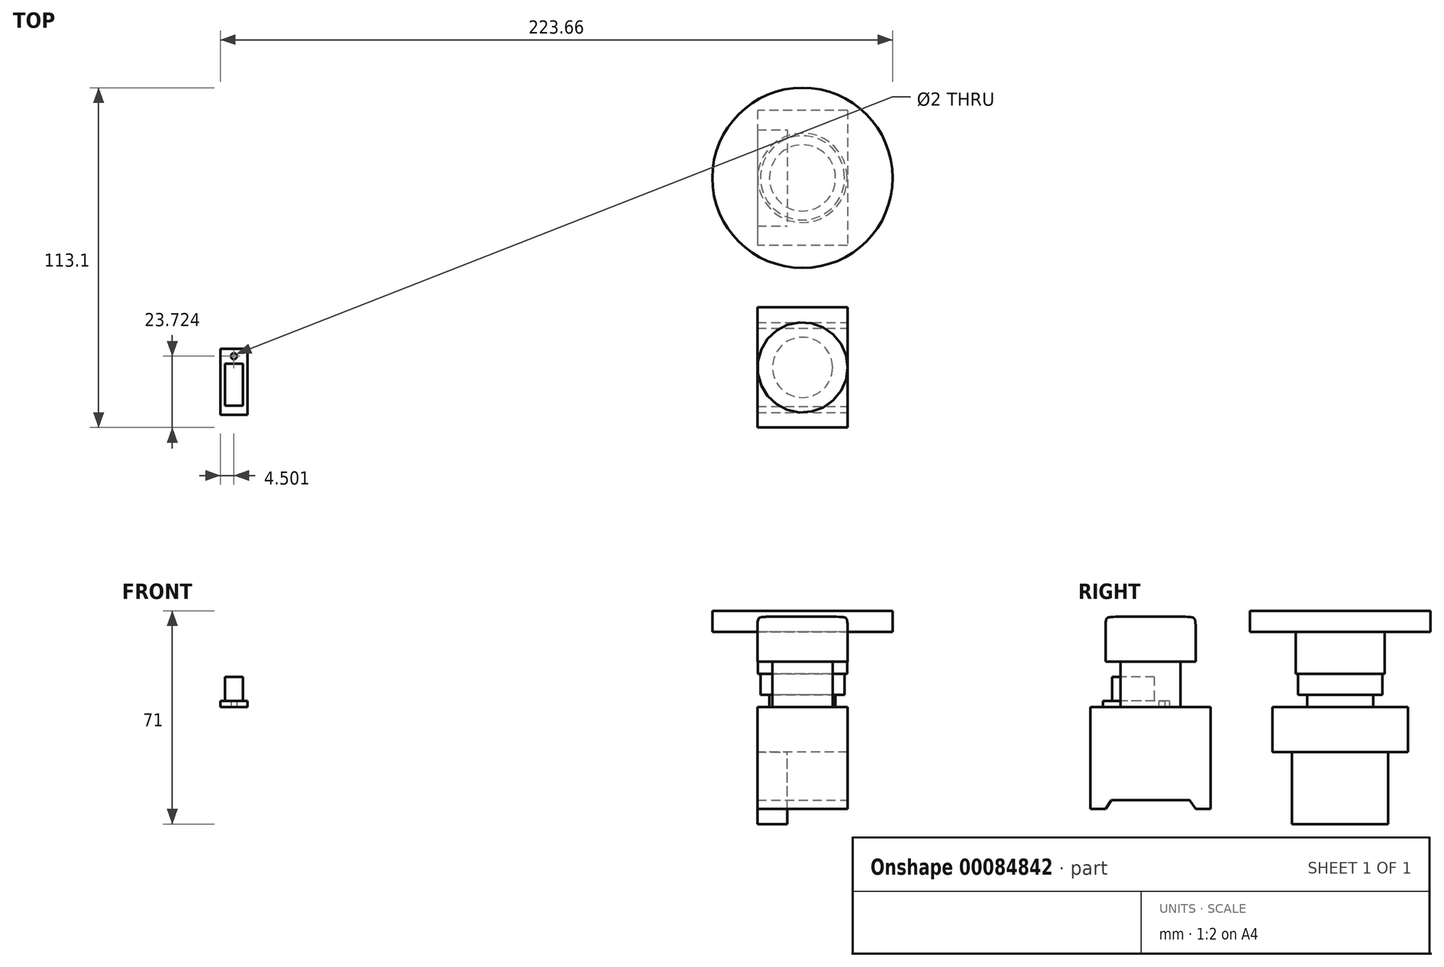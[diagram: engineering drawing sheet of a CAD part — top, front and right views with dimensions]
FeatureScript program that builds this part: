
annotation { "Feature Type Name" : "Feature", "Feature Type Description" : "" }
export const myFeature = defineFeature(function(context is Context, id is Id, definition is map)
    precondition{}
    {
        {
            var Q0;
            Q0=qCreatedBy(makeId("Front.planeOp"),FACE);
            var sketch = newSketch(context, id + "F0", { "sketchPlane" : qUnion([Q0])});
            skLineSegment(sketch, "E0", {"start": v(0, 0) * mm, "end": v(10, 0) * mm});
            skLineSegment(sketch, "E1", {"start": v(10, 0) * mm, "end": v(10, 15) * mm});
            skLineSegment(sketch, "E2", {"start": v(10, 15) * mm, "end": v(15, 15) * mm});
            skLineSegment(sketch, "E3", {"start": v(15, 15) * mm, "end": v(15, 30) * mm});
            skLineSegment(sketch, "E4", {"start": v(15, 30) * mm, "end": v(0, 30) * mm});
            skLineSegment(sketch, "E5", {"start": v(0, 30) * mm, "end": v(0, 0) * mm});
            skSolve(sketch);
        }
        {
            var Q0;
            Q0=qSketchRegion(id+"F0",true);
            var Q1;
            Q1=sQuery(id+"F0.wireOp",EDGE,"E5");
            revolve(context, id + "F1", {"entities" : qUnion([Q0]), "axis" : qUnion([Q1]), "revolveType" : RevolveType.FULL});
        }
        {
            var Q0;
            Q0=makeQuery(id+"F1.opRevolve","SWEPT_EDGE",EDGE,{"disambiguationData":[OSD([sQuery(id+"F0.wireOp",EDGE,"E3"),sQuery(id+"F0.wireOp",EDGE,"E4")])]});
            fillet(context, id + "F2", {"entities" : qUnion([Q0]), "radius" : 5 * mm, "tangentPropagation" : true, "rho" : 0.8, "crossSection" : FilletCrossSection.CONIC, "allowEdgeOverflow" : false});
        }
        {
            var Q0;
            Q0=qCreatedBy(makeId("Top.planeOp"),FACE);
            var sketch = newSketch(context, id + "F3", { "sketchPlane" : qUnion([Q0])});
            skLineSegment(sketch, "E6.rect.bottom", {"start": v(15, 20) * mm, "end": v(-15, 20) * mm});
            skLineSegment(sketch, "E6.rect.top", {"start": v(15, -20) * mm, "end": v(-15, -20) * mm});
            skLineSegment(sketch, "E6.rect.left", {"start": v(15, 20) * mm, "end": v(15, -20) * mm});
            skLineSegment(sketch, "E6.rect.right", {"start": v(-15, 20) * mm, "end": v(-15, -20) * mm});
            skPoint(sketch, "E6.rect.middle", {"position": v(0, 0) * mm});
            skSolve(sketch);
        }
        {
            var Q0;
            Q0=qSketchRegion(id+"F3",true);
            extrude(context, id + "F4", {"entities" : qUnion([Q0]), "operationType" : NewBodyOperationType.ADD, "oppositeDirection" : true, "depth" : 34 * mm});
        }
        {
            var Q0;
            Q0=makeQuery(id+"F4.opExtrude","SWEPT_FACE",FACE,{"disambiguationData":[OSD([sQuery(id+"F3.wireOp",EDGE,"E6.rect.left")])]});
            var sketch = newSketch(context, id + "F5", { "sketchPlane" : qUnion([Q0])});
            skLineSegment(sketch, "E7", {"start": v(0, -34) * mm, "end": v(-15, -34) * mm});
            skLineSegment(sketch, "E8", {"start": v(-15, -34) * mm, "end": v(-13, -31) * mm});
            skLineSegment(sketch, "E9", {"start": v(-13, -31) * mm, "end": v(0, -31) * mm});
            skLineSegment(sketch, "E10.MirrorCS", {"start": v(0, -34) * mm, "end": v(15, -34) * mm});
            skLineSegment(sketch, "E11.MirrorCS", {"start": v(13, -31) * mm, "end": v(0, -31) * mm});
            skLineSegment(sketch, "E12.MirrorCS", {"start": v(15, -34) * mm, "end": v(13, -31) * mm});
            skSolve(sketch);
        }
        {
            var Q0;
            Q0=qSketchRegion(id+"F5",true);
            extrude(context, id + "F6", {"entities" : qUnion([Q0]), "operationType" : NewBodyOperationType.REMOVE, "oppositeDirection" : true, "depth" : 34 * mm});
        }
        {
            var Q0;
            Q0=qCreatedBy(makeId("Top.planeOp"),FACE);
            var sketch = newSketch(context, id + "F7", { "sketchPlane" : qUnion([Q0])});
            skLineSegment(sketch, "E13.bottom", {"start": v(-193.66, 6.22) * mm, "end": v(-184.66, 6.22) * mm});
            skLineSegment(sketch, "E13.top", {"start": v(-193.66, -15.78) * mm, "end": v(-184.66, -15.78) * mm});
            skLineSegment(sketch, "E13.left", {"start": v(-193.66, 6.22) * mm, "end": v(-193.66, -15.78) * mm});
            skLineSegment(sketch, "E13.right", {"start": v(-184.66, 6.22) * mm, "end": v(-184.66, -15.78) * mm});
            skPoint(sketch, "E14", {"position": v(-189.16, 6.22) * mm});
            skLineSegment(sketch, "E15", {"start": v(-189.16, 6.22) * mm, "end": v(-189.16, 0.64) * mm, "construction": true});
            skCircle(sketch, "E16", {"center": v(-189.16, 3.72) * mm, "radius": 1 * mm});
            skSolve(sketch);
        }
        {
            var Q0;
            Q0=qSketchRegion(id+"F7",true);
            extrude(context, id + "F8", {"entities" : qUnion([Q0]), "depth" : 2 * mm});
        }
        {
            var Q0;
            Q0=makeQuery(id+"F8.opExtrude","CAP_FACE",FACE,{"disambiguationData":[OSD([sQuery(id+"F7.wireOp",EDGE,"E13.bottom"),sQuery(id+"F7.wireOp",EDGE,"E13.top"),sQuery(id+"F7.wireOp",EDGE,"E13.left"),sQuery(id+"F7.wireOp",EDGE,"E13.right")])],"isStart":false});
            var sketch = newSketch(context, id + "F9", { "sketchPlane" : qUnion([Q0])});
            skLineSegment(sketch, "E17", {"start": v(-193.66, -5.78) * mm, "end": v(-184.66, -5.78) * mm, "construction": true});
            skPoint(sketch, "E18", {"position": v(-189.16, -5.78) * mm});
            skLineSegment(sketch, "E19.rect.bottom", {"start": v(-186.16, 1.22) * mm, "end": v(-192.16, 1.22) * mm});
            skLineSegment(sketch, "E19.rect.top", {"start": v(-186.16, -12.78) * mm, "end": v(-192.16, -12.78) * mm});
            skLineSegment(sketch, "E19.rect.left", {"start": v(-186.16, 1.22) * mm, "end": v(-186.16, -12.78) * mm});
            skLineSegment(sketch, "E19.rect.right", {"start": v(-192.16, 1.22) * mm, "end": v(-192.16, -12.78) * mm});
            skSolve(sketch);
        }
        {
            var Q0;
            Q0=makeQuery(id+"F9.imprint","IMPRINT",FACE,{"disambiguationData":[TD([[makeQuery(id+"F9.imprint","IMPRINT",EDGE,{"derivedFrom":sQuery(id+"F9.wireOp",EDGE,"E19.rect.bottom")}),1.0]])]});
            extrude(context, id + "F10", {"entities" : qUnion([Q0]), "operationType" : NewBodyOperationType.ADD, "depth" : 8 * mm});
        }
        {
            var Q0;
            Q0=qCreatedBy(makeId("Top.planeOp"),FACE);
            var sketch = newSketch(context, id + "F11", { "sketchPlane" : qUnion([Q0])});
            skLineSegment(sketch, "E20.bottom", {"start": v(15, 85.6) * mm, "end": v(-15, 85.6) * mm});
            skLineSegment(sketch, "E20.top", {"start": v(15, 40.6) * mm, "end": v(-15, 40.6) * mm});
            skLineSegment(sketch, "E20.left", {"start": v(15, 85.6) * mm, "end": v(15, 40.6) * mm});
            skLineSegment(sketch, "E20.right", {"start": v(-15, 85.6) * mm, "end": v(-15, 40.6) * mm});
            skPoint(sketch, "E20.middle", {"position": v(0, 63.1) * mm});
            skSolve(sketch);
        }
        {
            var Q0;
            Q0=qSketchRegion(id+"F11",true);
            extrude(context, id + "F12", {"entities" : qUnion([Q0]), "oppositeDirection" : true, "depth" : 15 * mm});
        }
        {
            var Q0;
            Q0=makeQuery(id+"F12.opExtrude","CAP_FACE",FACE,{"disambiguationData":[OSD([sQuery(id+"F11.wireOp",EDGE,"E20.bottom"),sQuery(id+"F11.wireOp",EDGE,"E20.top"),sQuery(id+"F11.wireOp",EDGE,"E20.left"),sQuery(id+"F11.wireOp",EDGE,"E20.right")])],"isStart":false});
            var sketch = newSketch(context, id + "F13", { "sketchPlane" : qUnion([Q0])});
            skLineSegment(sketch, "E21", {"start": v(-15, -63.1) * mm, "end": v(15, -63.1) * mm, "construction": true});
            skLineSegment(sketch, "E22.bottom", {"start": v(-15, -79.1) * mm, "end": v(-5, -79.1) * mm});
            skLineSegment(sketch, "E22.top", {"start": v(-15, -47.1) * mm, "end": v(-5, -47.1) * mm});
            skLineSegment(sketch, "E22.left", {"start": v(-15, -79.1) * mm, "end": v(-15, -47.1) * mm});
            skLineSegment(sketch, "E22.right", {"start": v(-5, -79.1) * mm, "end": v(-5, -47.1) * mm});
            skPoint(sketch, "E22.middle", {"position": v(-10, -63.1) * mm});
            skSolve(sketch);
        }
        {
            var Q0;
            Q0=qSketchRegion(id+"F13",true);
            extrude(context, id + "F14", {"entities" : qUnion([Q0]), "operationType" : NewBodyOperationType.ADD, "depth" : 24 * mm});
        }
        {
            var Q0;
            Q0=makeQuery(id+"F12.opExtrude","CAP_FACE",FACE,{"disambiguationData":[OSD([sQuery(id+"F11.wireOp",EDGE,"E20.bottom"),sQuery(id+"F11.wireOp",EDGE,"E20.top"),sQuery(id+"F11.wireOp",EDGE,"E20.left"),sQuery(id+"F11.wireOp",EDGE,"E20.right")])],"isStart":true});
            var sketch = newSketch(context, id + "F15", { "sketchPlane" : qUnion([Q0])});
            skLineSegment(sketch, "E23", {"start": v(0, 85.6) * mm, "end": v(0, 40.6) * mm, "construction": true});
            skLineSegment(sketch, "E24", {"start": v(-15, 63.1) * mm, "end": v(15, 63.1) * mm, "construction": true});
            skPoint(sketch, "E25", {"position": v(0, 63.1) * mm});
            skCircle(sketch, "E26", {"center": v(0, 63.1) * mm, "radius": 11 * mm});
            skSolve(sketch);
        }
        {
            var Q0;
            Q0=qSketchRegion(id+"F15",true);
            extrude(context, id + "F16", {"entities" : qUnion([Q0]), "operationType" : NewBodyOperationType.ADD, "depth" : 4 * mm});
        }
        {
            var Q0;
            Q0=makeQuery(id+"F16.opExtrude","CAP_FACE",FACE,{"disambiguationData":[OSD([sQuery(id+"F15.wireOp",EDGE,"E26")])],"isStart":false});
            var sketch = newSketch(context, id + "F17", { "sketchPlane" : qUnion([Q0])});
            skPoint(sketch, "E27", {"position": v(0, 63.1) * mm});
            skCircle(sketch, "E28", {"center": v(0, 63.1) * mm, "radius": 14 * mm});
            skSolve(sketch);
        }
        {
            var Q0;
            Q0=qSketchRegion(id+"F17",true);
            extrude(context, id + "F18", {"entities" : qUnion([Q0]), "operationType" : NewBodyOperationType.ADD, "depth" : 7 * mm});
        }
        {
            var Q0;
            Q0=makeQuery(id+"F18.opExtrude","CAP_FACE",FACE,{"disambiguationData":[OSD([sQuery(id+"F17.wireOp",EDGE,"E28")])],"isStart":false});
            var sketch = newSketch(context, id + "F19", { "sketchPlane" : qUnion([Q0])});
            skPoint(sketch, "E29", {"position": v(0, 63.1) * mm});
            skCircle(sketch, "E30", {"center": v(0, 63.1) * mm, "radius": 14.85 * mm});
            skSolve(sketch);
        }
        {
            var Q0;
            Q0=qSketchRegion(id+"F19",true);
            extrude(context, id + "F20", {"entities" : qUnion([Q0]), "operationType" : NewBodyOperationType.ADD, "depth" : 14 * mm});
        }
        {
            var Q0;
            Q0=makeQuery(id+"F20.opExtrude","CAP_FACE",FACE,{"disambiguationData":[OSD([sQuery(id+"F19.wireOp",EDGE,"E30")])],"isStart":false});
            var sketch = newSketch(context, id + "F21", { "sketchPlane" : qUnion([Q0])});
            skPoint(sketch, "E31", {"position": v(0, 63.1) * mm});
            skCircle(sketch, "E32", {"center": v(0, 63.1) * mm, "radius": 30 * mm});
            skSolve(sketch);
        }
        {
            var Q0;
            Q0=qSketchRegion(id+"F21",true);
            extrude(context, id + "F22", {"entities" : qUnion([Q0]), "operationType" : NewBodyOperationType.ADD, "depth" : 7 * mm});
        }
    });
